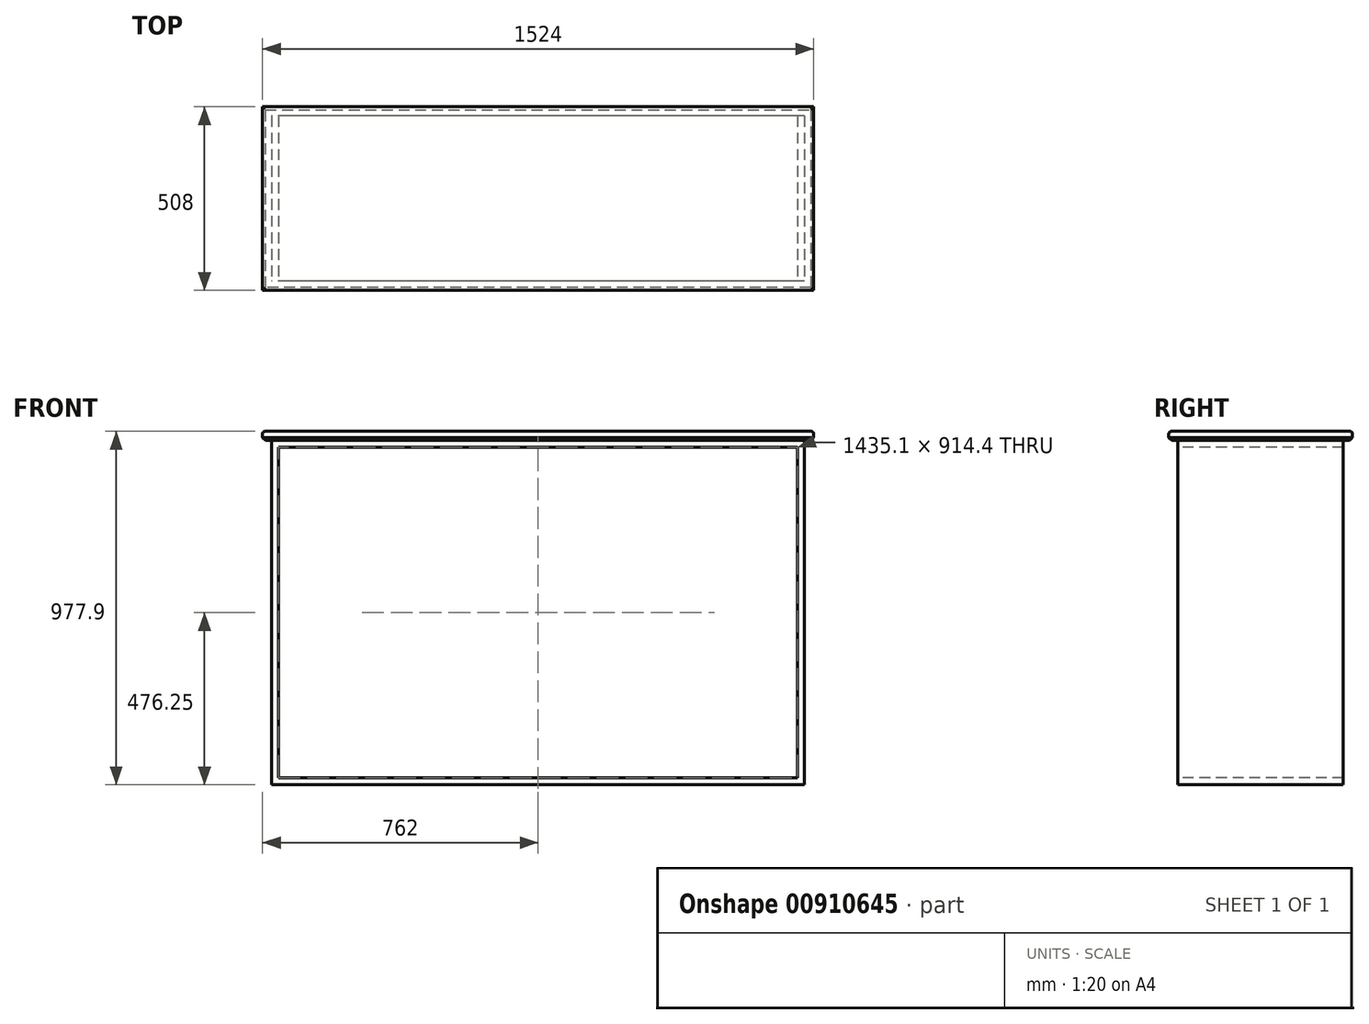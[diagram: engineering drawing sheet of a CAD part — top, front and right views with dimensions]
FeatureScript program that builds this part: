
annotation { "Feature Type Name" : "Feature", "Feature Type Description" : "" }
export const myFeature = defineFeature(function(context is Context, id is Id, definition is map)
    precondition{}
    {
        {
            var Q0;
            Q0=qCreatedBy(makeId("Top.planeOp"),FACE);
            var sketch = newSketch(context, id + "F0", { "sketchPlane" : qUnion([Q0])});
            skLineSegment(sketch, "E0.bottom", {"start": v(762, -254) * mm, "end": v(-762, -254) * mm});
            skLineSegment(sketch, "E0.top", {"start": v(762, 254) * mm, "end": v(-762, 254) * mm});
            skLineSegment(sketch, "E0.left", {"start": v(762, -254) * mm, "end": v(762, 254) * mm});
            skLineSegment(sketch, "E0.right", {"start": v(-762, -254) * mm, "end": v(-762, 254) * mm});
            skPoint(sketch, "E0.middle", {"position": v(0, 0) * mm});
            skSolve(sketch);
        }
        {
            var Q0;
            Q0 = qSketchRegion(id + "F0", true);
            extrude(context, id + "F1", {"entities" : qUnion([Q0]), "depth" : 25.4 * mm, "offsetDistance" : 25.4 * mm});
        }
        {
            var Q0;
            Q0=makeQuery(id+"F1.opExtrude","CAP_FACE",FACE,{"disambiguationData":[OSD([sQuery(id+"F0.wireOp",EDGE,"E0.bottom"),sQuery(id+"F0.wireOp",EDGE,"E0.top"),sQuery(id+"F0.wireOp",EDGE,"E0.left"),sQuery(id+"F0.wireOp",EDGE,"E0.right")])],"isStart":true});
            var sketch = newSketch(context, id + "F2", { "sketchPlane" : qUnion([Q0])});
            skLineSegment(sketch, "E1.bottom", {"start": v(736.6, -228.6) * mm, "end": v(-736.6, -228.6) * mm});
            skLineSegment(sketch, "E1.top", {"start": v(736.6, 228.6) * mm, "end": v(-736.6, 228.6) * mm});
            skLineSegment(sketch, "E1.left", {"start": v(736.6, -228.6) * mm, "end": v(736.6, 228.6) * mm});
            skLineSegment(sketch, "E1.right", {"start": v(-736.6, -228.6) * mm, "end": v(-736.6, 228.6) * mm});
            skPoint(sketch, "E1.middle", {"position": v(0, 0) * mm});
            skSolve(sketch);
        }
        {
            var Q0;
            Q0 = qSketchRegion(id + "F2", true);
            extrude(context, id + "F3", {"entities" : qUnion([Q0]), "operationType" : NewBodyOperationType.ADD, "depth" : 19.05 * mm, "offsetDistance" : 25.4 * mm});
        }
        {
            var Q0;
            Q0=makeQuery(id+"F1.opExtrude","CAP_EDGE",EDGE,{"disambiguationData":[OSD([sQuery(id+"F0.wireOp",EDGE,"E0.bottom")])],"isStart":true});
            var Q1;
            Q1=makeQuery(id+"F1.opExtrude","CAP_EDGE",EDGE,{"disambiguationData":[OSD([sQuery(id+"F0.wireOp",EDGE,"E0.left")])],"isStart":true});
            var Q2;
            Q2=makeQuery(id+"F1.opExtrude","CAP_EDGE",EDGE,{"disambiguationData":[OSD([sQuery(id+"F0.wireOp",EDGE,"E0.top")])],"isStart":true});
            var Q3;
            Q3=makeQuery(id+"F1.opExtrude","CAP_EDGE",EDGE,{"disambiguationData":[OSD([sQuery(id+"F0.wireOp",EDGE,"E0.right")])],"isStart":true});
            chamfer(context, id + "F4", {"entities" : qUnion([Q0, Q1, Q2, Q3]), "width" : 8.38 * mm, "tangentPropagation" : true});
        }
        {
            var Q0;
            Q0=makeQuery(id+"F1.opExtrude","CAP_EDGE",EDGE,{"disambiguationData":[OSD([sQuery(id+"F0.wireOp",EDGE,"E0.bottom")])],"isStart":false});
            var Q1;
            Q1=makeQuery(id+"F1.opExtrude","CAP_EDGE",EDGE,{"disambiguationData":[OSD([sQuery(id+"F0.wireOp",EDGE,"E0.top")])],"isStart":false});
            var Q2;
            Q2=makeQuery(id+"F1.opExtrude","CAP_EDGE",EDGE,{"disambiguationData":[OSD([sQuery(id+"F0.wireOp",EDGE,"E0.left")])],"isStart":false});
            var Q3;
            Q3=makeQuery(id+"F1.opExtrude","CAP_EDGE",EDGE,{"disambiguationData":[OSD([sQuery(id+"F0.wireOp",EDGE,"E0.right")])],"isStart":false});
            fillet(context, id + "F5", {"entities" : qUnion([Q0, Q1, Q2, Q3]), "radius" : 6.35 * mm, "tangentPropagation" : true, "allowEdgeOverflow" : false});
        }
        {
            var Q0;
            Q0=makeQuery(id+"F3.opExtrude","CAP_FACE",FACE,{"disambiguationData":[OSD([sQuery(id+"F2.wireOp",EDGE,"E1.bottom"),sQuery(id+"F2.wireOp",EDGE,"E1.top"),sQuery(id+"F2.wireOp",EDGE,"E1.left"),sQuery(id+"F2.wireOp",EDGE,"E1.right")])],"isStart":false});
            var sketch = newSketch(context, id + "F6", { "sketchPlane" : qUnion([Q0])});
            skLineSegment(sketch, "E2.bottom", {"start": v(736.6, -228.6) * mm, "end": v(717.55, -228.6) * mm});
            skLineSegment(sketch, "E2.top", {"start": v(736.6, 228.6) * mm, "end": v(717.55, 228.6) * mm});
            skLineSegment(sketch, "E2.left", {"start": v(736.6, -228.6) * mm, "end": v(736.6, 228.6) * mm});
            skLineSegment(sketch, "E2.right", {"start": v(717.55, -228.6) * mm, "end": v(717.55, 228.6) * mm});
            skLineSegment(sketch, "E3.bottom", {"start": v(-736.6, -228.6) * mm, "end": v(-717.55, -228.6) * mm});
            skLineSegment(sketch, "E3.top", {"start": v(-736.6, 228.6) * mm, "end": v(-717.55, 228.6) * mm});
            skLineSegment(sketch, "E3.left", {"start": v(-736.6, -228.6) * mm, "end": v(-736.6, 228.6) * mm});
            skLineSegment(sketch, "E3.right", {"start": v(-717.55, -228.6) * mm, "end": v(-717.55, 228.6) * mm});
            skSolve(sketch);
        }
        {
            var Q0;
            Q0 = qSketchRegion(id + "F6", true);
            extrude(context, id + "F7", {"entities" : qUnion([Q0]), "operationType" : NewBodyOperationType.ADD, "depth" : 914.4 * mm, "offsetDistance" : 25.4 * mm});
        }
        {
            var Q0;
            Q0=makeQuery(id+"F7.opExtrude","CAP_FACE",FACE,{"disambiguationData":[OSD([sQuery(id+"F6.wireOp",EDGE,"E3.bottom"),sQuery(id+"F6.wireOp",EDGE,"E3.top"),sQuery(id+"F6.wireOp",EDGE,"E3.left"),sQuery(id+"F6.wireOp",EDGE,"E3.right")])],"isStart":false});
            var sketch = newSketch(context, id + "F8", { "sketchPlane" : qUnion([Q0])});
            skLineSegment(sketch, "E4.bottom", {"start": v(-736.6, -228.6) * mm, "end": v(736.6, -228.6) * mm});
            skLineSegment(sketch, "E4.top", {"start": v(-736.6, 228.6) * mm, "end": v(736.6, 228.6) * mm});
            skLineSegment(sketch, "E4.left", {"start": v(-736.6, -228.6) * mm, "end": v(-736.6, 228.6) * mm});
            skLineSegment(sketch, "E4.right", {"start": v(736.6, -228.6) * mm, "end": v(736.6, 228.6) * mm});
            skSolve(sketch);
        }
        {
            var Q0;
            Q0 = qSketchRegion(id + "F8", true);
            extrude(context, id + "F9", {"entities" : qUnion([Q0]), "operationType" : NewBodyOperationType.ADD, "depth" : 19.05 * mm, "offsetDistance" : 25.4 * mm});
        }
    });
